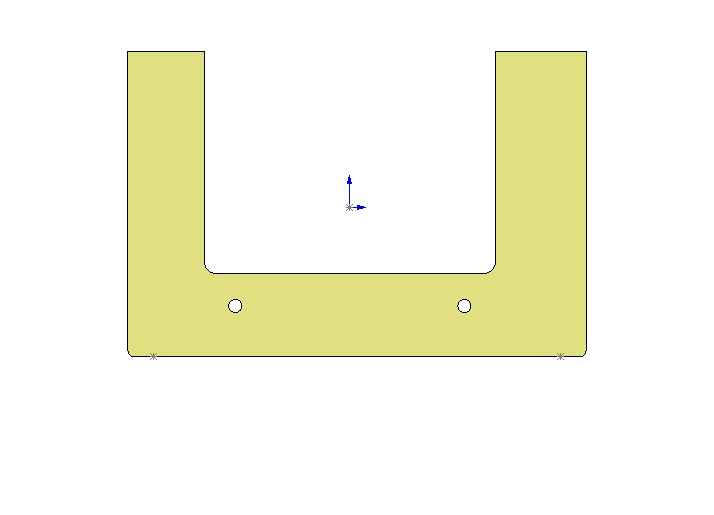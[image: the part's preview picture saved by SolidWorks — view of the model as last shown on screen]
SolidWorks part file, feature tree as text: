
SOLIDWORKS PART (.sldprt)
format: sldprt  version: not decoded by parser v0  size: 341,504 bytes
history: native  units: mm
features: sketch x7, thread x6, hole x3, extrude x1, fillet x1 (+10 scaffold rows collapsed)
feature tree (28):
  scaffold x10  (default folders/planes/origin — collapsed)
  sketch  "Sketch1"  dims[c1.D6=6.35mm c1.D1=3.175mm c1.D2=3.175mm c1.D3=38.1mm c1.D4=38.1mm c1.D5=1.27mm c2.D6=189.738mm c2.D7=12.7mm c2.D4=228.6mm]
  extrude  "Extrude1"  Depth=19.05mm
  hole  "5/16-18 Tapped Hole1"  Diameter=6.5278mm Depth=22.9235mm
  sketch  "Sketch3"  dims[D1=12.7mm D2=6.35mm D3=6.35mm D4=12.7mm]
  sketch  "Sketch2"  dims[hole-wizard template sketch: 47 standard entries collapsed; hole parameters kept: c15.Tap Drill Depth=22.9235mm c15.D3=~14.816244mm c15.Drill Angle=118.0deg]
  thread  "Cosmetic Thread1"  Diameter=15.875mm  [1 undecoded]
  thread  "Cosmetic Thread2"  Diameter=15.875mm  [1 undecoded]
  hole  "#6-32 Tapped Hole3"  Diameter=2.7051mm Depth=10.973003mm
  sketch  "Sketch9"  dims[D1=12.7mm D2=12.7mm]
  sketch  "Sketch8"  dims[hole-wizard template sketch: 47 standard entries collapsed; hole parameters kept: c15.Tap Drill Depth=~10.973003mm c15.D3=~14.816244mm c15.Drill Angle=118.0deg]
  thread  "Cosmetic Thread9"  Diameter=7.009994mm  [1 undecoded]
  thread  "Cosmetic Thread10"  Diameter=7.009994mm  [1 undecoded]
  hole  "1/4-20 Tapped Hole2"  Diameter=6.5278mm Depth=22.9235mm
  sketch  "Sketch11"
  sketch  "Sketch10"  dims[hole-wizard template sketch: 47 standard entries collapsed; hole parameters kept: c15.Tap Drill Depth=22.9235mm c15.D3=~14.816244mm c15.Drill Angle=118.0deg]
  thread  "Cosmetic Thread11"  Diameter=15.875mm  [1 undecoded]
  thread  "Cosmetic Thread12"  Diameter=15.875mm  [1 undecoded]
  fillet  "Fillet1"  Radius=3.175mm
decode coverage: 17 of 18 modeling features carry decoded parameters
note: ~ marks probable driven/reference dimensions
note: 6 parameter values undecoded
note: suppression state not decoded; provenance and decode notes live in map.json
